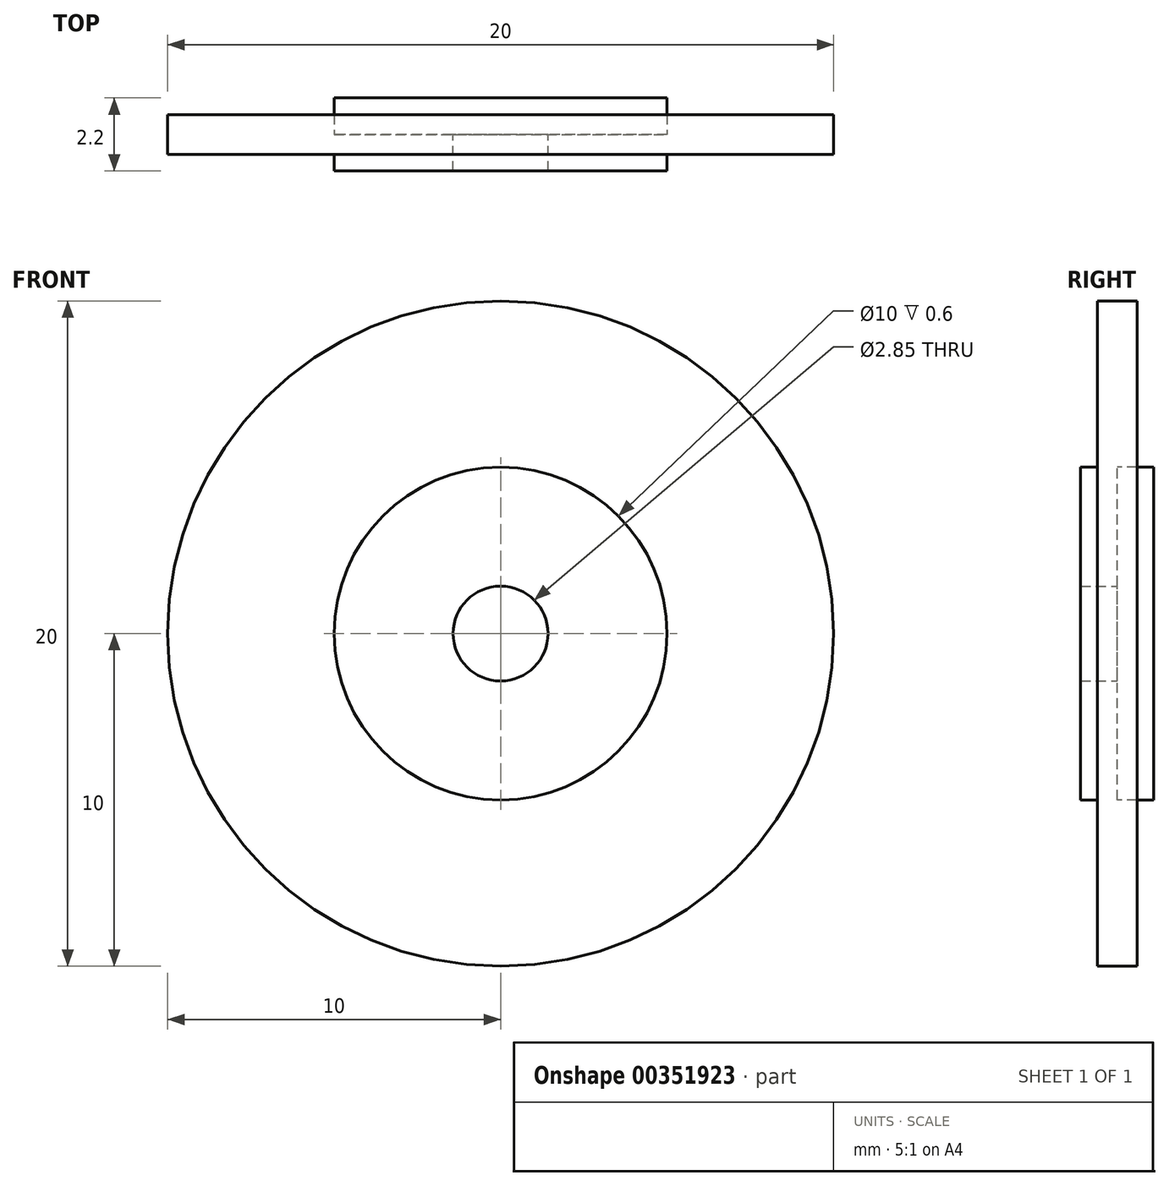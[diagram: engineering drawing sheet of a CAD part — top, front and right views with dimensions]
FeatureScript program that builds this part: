
annotation { "Feature Type Name" : "Feature", "Feature Type Description" : "" }
export const myFeature = defineFeature(function(context is Context, id is Id, definition is map)
    precondition{}
    {
        {
            var Q0;
            Q0=qCreatedBy(makeId("Front.planeOp"),FACE);
            var sketch = newSketch(context, id + "F0", { "sketchPlane" : qUnion([Q0])});
            skCircle(sketch, "E0", {"center": v(0, 0) * mm, "radius": 10 * mm});
            skCircle(sketch, "E1", {"center": v(0, 0) * mm, "radius": 5 * mm});
            skSolve(sketch);
        }
        {
            var Q0;
            Q0=makeQuery(id+"F0.imprint","IMPRINT",FACE,{"disambiguationData":[TD([[makeQuery(id+"F0.imprint","IMPRINT",EDGE,{"derivedFrom":sQuery(id+"F0.wireOp",EDGE,"E1")}),1.0]])]});
            extrude(context, id + "F1", {"entities" : qUnion([Q0]), "depth" : 1.1 * mm});
        }
        {
            var Q0;
            Q0=makeQuery(id+"F0.imprint","IMPRINT",FACE,{"disambiguationData":[TD([[makeQuery(id+"F0.imprint","IMPRINT",EDGE,{"derivedFrom":sQuery(id+"F0.wireOp",EDGE,"E0")}),1.0]])]});
            extrude(context, id + "F2", {"entities" : qUnion([Q0]), "depth" : .6 * mm});
        }
        {
            var Q0;
            Q0=makeQuery(id+"F0.imprint","IMPRINT",FACE,{"disambiguationData":[TD([[makeQuery(id+"F0.imprint","IMPRINT",EDGE,{"derivedFrom":sQuery(id+"F0.wireOp",EDGE,"E0")}),1.0]])]});
            extrude(context, id + "F3", {"entities" : qUnion([Q0]), "operationType" : NewBodyOperationType.ADD, "oppositeDirection" : true, "depth" : .6 * mm});
        }
        {
            var Q0;
            Q0=makeQuery(id+"F0.imprint","IMPRINT",FACE,{"disambiguationData":[TD([[makeQuery(id+"F0.imprint","IMPRINT",EDGE,{"derivedFrom":sQuery(id+"F0.wireOp",EDGE,"E1")}),1.0]])]});
            extrude(context, id + "F4", {"entities" : qUnion([Q0]), "oppositeDirection" : true, "depth" : 1.1 * mm});
        }
        {
            var Q0;
            Q0=makeQuery(id+"F4.opExtrude","CAP_FACE",FACE,{"disambiguationData":[OSD([sQuery(id+"F0.wireOp",EDGE,"E1")])],"isStart":false});
            cPlane(context, id + "F5", {"entities" : qUnion([Q0]), "cplaneType" : CPlaneType.OFFSET, "offset" : 0 * mm, "width" : 150 * mm, "height" : 150 * mm});
        }
        {
            var Q0;
            Q0=qCreatedBy(id+"F5.planeOp",FACE);
            var sketch = newSketch(context, id + "F6", { "sketchPlane" : qUnion([Q0])});
            skPoint(sketch, "E2", {"position": v(0, 0) * mm});
            skSolve(sketch);
        }
        {
            var Q0;
            Q0=sQuery(id+"F6.wireOp",VERTEX,"E2");
            var Q1;
            Q1=makeQuery(id+"F1.opExtrude","SWEPT_BODY",BODY,{"disambiguationData":[OSD([sQuery(id+"F0.wireOp",EDGE,"E1")])]});
            hole(context, id + "F7", {"style" : HoleStyle.SIMPLE, "endStyle" : HoleEndStyle.BLIND, "holeDiameter" : 2.85 * mm, "holeDepth" : 2.5 * mm, "isTappedThrough" : true, "tappedDepth" : 12 * mm, "tapClearance" : 3, "startFromSketch" : true, "locations" : qUnion([Q0]), "scope" : qUnion([Q1])});
        }
    });
